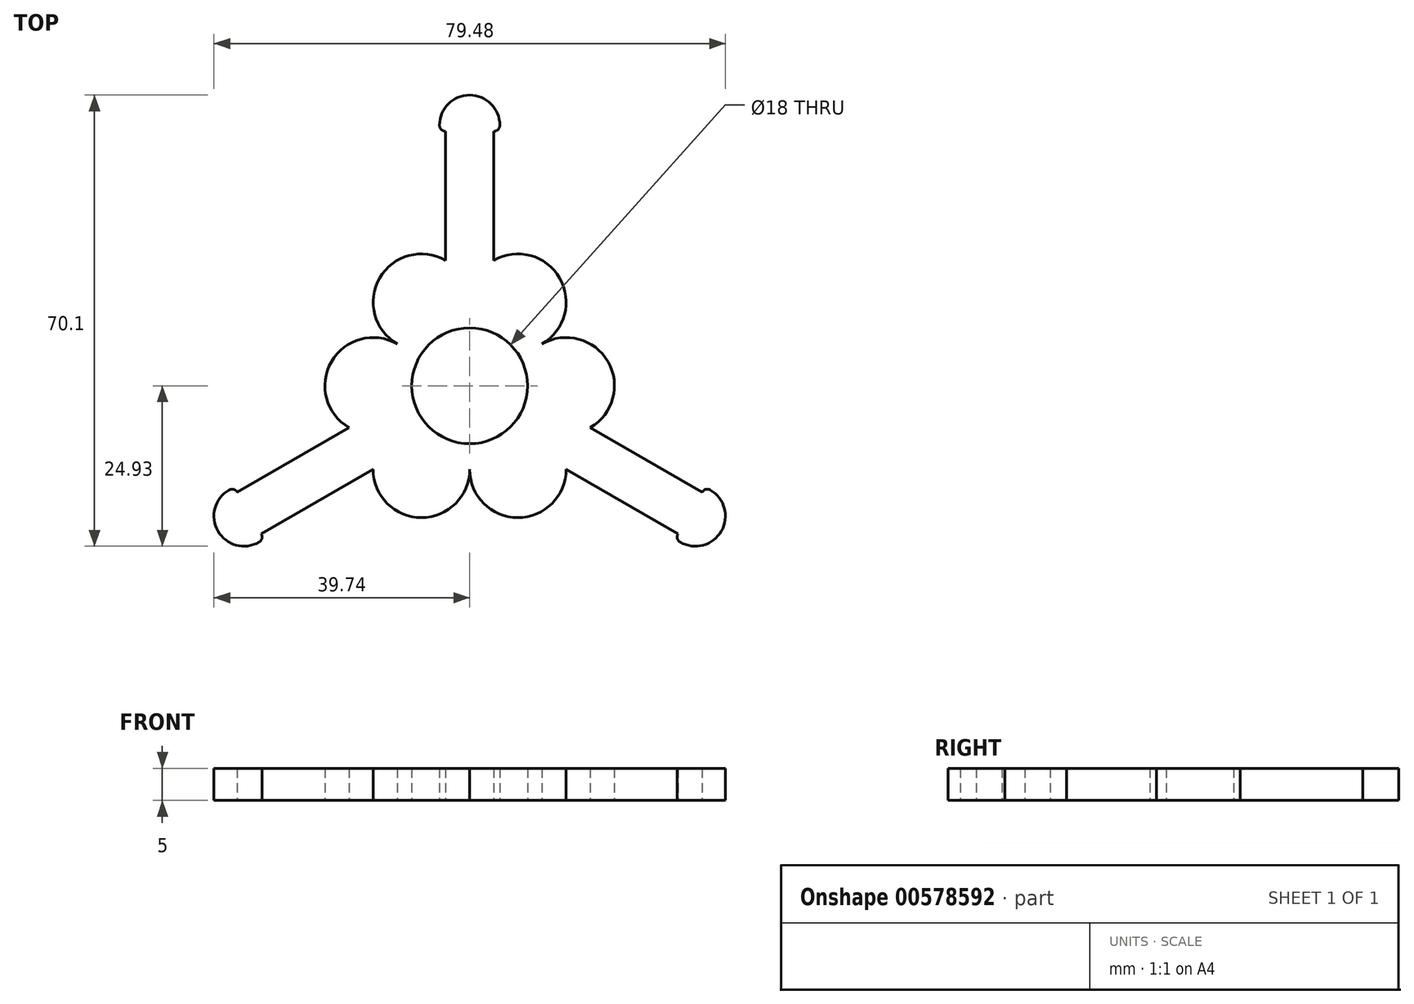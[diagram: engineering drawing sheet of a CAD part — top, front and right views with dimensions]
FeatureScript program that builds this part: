
annotation { "Feature Type Name" : "Feature", "Feature Type Description" : "" }
export const myFeature = defineFeature(function(context is Context, id is Id, definition is map)
    precondition{}
    {
        {
            var Q0;
            Q0=qCreatedBy(makeId("Top.planeOp"),FACE);
            var sketch = newSketch(context, id + "F0", { "sketchPlane" : qUnion([Q0])});
            skArc(sketch, "E0", {"start": v(-13.12, 7.26) * mm, "mid": v(-13, -7.5) * mm, "end": v(-0.27, -15) * mm});
            skArc(sketch, "E1.1.0", {"start": v(-3.75, 19.49) * mm, "mid": v(-14, 16.74) * mm, "end": v(-11.25, 6.5) * mm});
            skLineSegment(sketch, "E1.1.1", {"start": v(3.75, 19.49) * mm, "end": v(3.75, 39.54) * mm});
            skPoint(sketch, "E1.1.2", {"position": v(-3.75, 13) * mm});
            skArc(sketch, "E1.1.3", {"start": v(4.69, 40.48) * mm, "mid": v(0, 45.17) * mm, "end": v(-4.69, 40.48) * mm});
            skLineSegment(sketch, "E1.1.4", {"start": v(-3.75, 19.49) * mm, "end": v(-3.75, 39.54) * mm});
            skPoint(sketch, "E1.1.5", {"position": v(3.75, 13) * mm});
            skArc(sketch, "E1.1.6", {"start": v(3.75, 39.54) * mm, "mid": v(4.41, 39.82) * mm, "end": v(4.69, 40.48) * mm});
            skArc(sketch, "E1.1.7", {"start": v(-4.69, 40.48) * mm, "mid": v(-4.41, 39.82) * mm, "end": v(-3.75, 39.54) * mm});
            skArc(sketch, "E1.1.8", {"start": v(11.25, 6.5) * mm, "mid": v(14, 16.74) * mm, "end": v(3.75, 19.49) * mm});
            skArc(sketch, "E2.1.0", {"start": v(-11.25, 6.5) * mm, "mid": v(-21.5, 3.75) * mm, "end": v(-18.75, -6.5) * mm});
            skPoint(sketch, "E2.1.1", {"position": v(-13.13, -3.25) * mm});
            skArc(sketch, "E2.1.2", {"start": v(-37.4, -16.18) * mm, "mid": v(-39.11, -22.58) * mm, "end": v(-32.71, -24.3) * mm});
            skLineSegment(sketch, "E2.1.3", {"start": v(-18.75, -6.5) * mm, "end": v(-36.12, -16.52) * mm});
            skPoint(sketch, "E2.1.4", {"position": v(-9.38, -9.74) * mm});
            skLineSegment(sketch, "E2.1.5", {"start": v(-15, -13) * mm, "end": v(-32.37, -23.02) * mm});
            skArc(sketch, "E2.1.6", {"start": v(-15, -13) * mm, "mid": v(-7.5, -20.5) * mm, "end": v(0, -13) * mm});
            skArc(sketch, "E2.1.7", {"start": v(-36.12, -16.52) * mm, "mid": v(-36.69, -16.09) * mm, "end": v(-37.4, -16.18) * mm});
            skArc(sketch, "E2.1.8", {"start": v(-32.71, -24.3) * mm, "mid": v(-32.28, -23.73) * mm, "end": v(-32.37, -23.02) * mm});
            skArc(sketch, "E2.2.0", {"start": v(0, -13) * mm, "mid": v(7.5, -20.5) * mm, "end": v(15, -13) * mm});
            skPoint(sketch, "E2.2.1", {"position": v(9.37, -9.74) * mm});
            skArc(sketch, "E2.2.2", {"start": v(32.71, -24.3) * mm, "mid": v(39.11, -22.58) * mm, "end": v(37.4, -16.18) * mm});
            skLineSegment(sketch, "E2.2.3", {"start": v(15, -13) * mm, "end": v(32.37, -23.02) * mm});
            skPoint(sketch, "E2.2.4", {"position": v(13.12, -3.25) * mm});
            skLineSegment(sketch, "E2.2.5", {"start": v(18.75, -6.5) * mm, "end": v(36.12, -16.52) * mm});
            skArc(sketch, "E2.2.6", {"start": v(18.75, -6.5) * mm, "mid": v(21.5, 3.75) * mm, "end": v(11.25, 6.5) * mm});
            skArc(sketch, "E2.2.7", {"start": v(32.37, -23.02) * mm, "mid": v(32.28, -23.73) * mm, "end": v(32.71, -24.3) * mm});
            skArc(sketch, "E2.2.8", {"start": v(37.4, -16.18) * mm, "mid": v(36.69, -16.09) * mm, "end": v(36.12, -16.52) * mm});
            skPoint(sketch, "E3.orphan", {"position": v(0, 13) * mm});
            skPoint(sketch, "E4.orphan", {"position": v(-11.25, -6.5) * mm});
            skPoint(sketch, "E5.orphan", {"position": v(11.25, -6.5) * mm});
            skArc(sketch, "E6.trimOffspring", {"start": v(12.85, 7.74) * mm, "mid": v(0, 15) * mm, "end": v(-12.85, 7.74) * mm});
            skArc(sketch, "E7.trimOffspring", {"start": v(0.27, -15) * mm, "mid": v(13, -7.5) * mm, "end": v(13.13, 7.26) * mm});
            skCircle(sketch, "E8", {"center": v(0, 0) * mm, "radius": 9 * mm});
            skSolve(sketch);
        }
        {
            var Q0;
            {var subQ1=sQuery(id+"F0.wireOp",EDGE,"E1.1.1");Q0=makeQuery(id+"F0.imprint","IMPRINT",FACE,{"disambiguationData":[TD([[makeQuery(id+"F0.imprint","IMPRINT",EDGE,{"derivedFrom":subQ1}),1.0]])]});}
            var Q1;
            Q1=makeQuery(id+"F0.imprint","IMPRINT",FACE,{"disambiguationData":[TD([[makeQuery(id+"F0.imprint","IMPRINT",EDGE,{"derivedFrom":sQuery(id+"F0.wireOp",EDGE,"E2.2.2")}),1.0]])]});
            var Q2;
            {var subQ11=sQuery(id+"F0.wireOp",EDGE,"E0");Q2=makeQuery(id+"F0.imprint","IMPRINT",FACE,{"disambiguationData":[TD([[makeQuery(id+"F0.imprint","IMPRINT",EDGE,{"derivedFrom":subQ11}),1.0]])]});}
            var Q3;
            {var subQ2=sQuery(id+"F0.wireOp",EDGE,"E0");Q3=makeQuery(id+"F0.imprint","IMPRINT",FACE,{"disambiguationData":[TD([[makeQuery(id+"F0.imprint","IMPRINT",EDGE,{"derivedFrom":subQ2}),-1.0]])]});}
            extrude(context, id + "F1", {"entities" : qUnion([Q0, Q1, Q2, Q3]), "depth" : 5 * mm, "offsetDistance" : 25 * mm});
        }
    });
